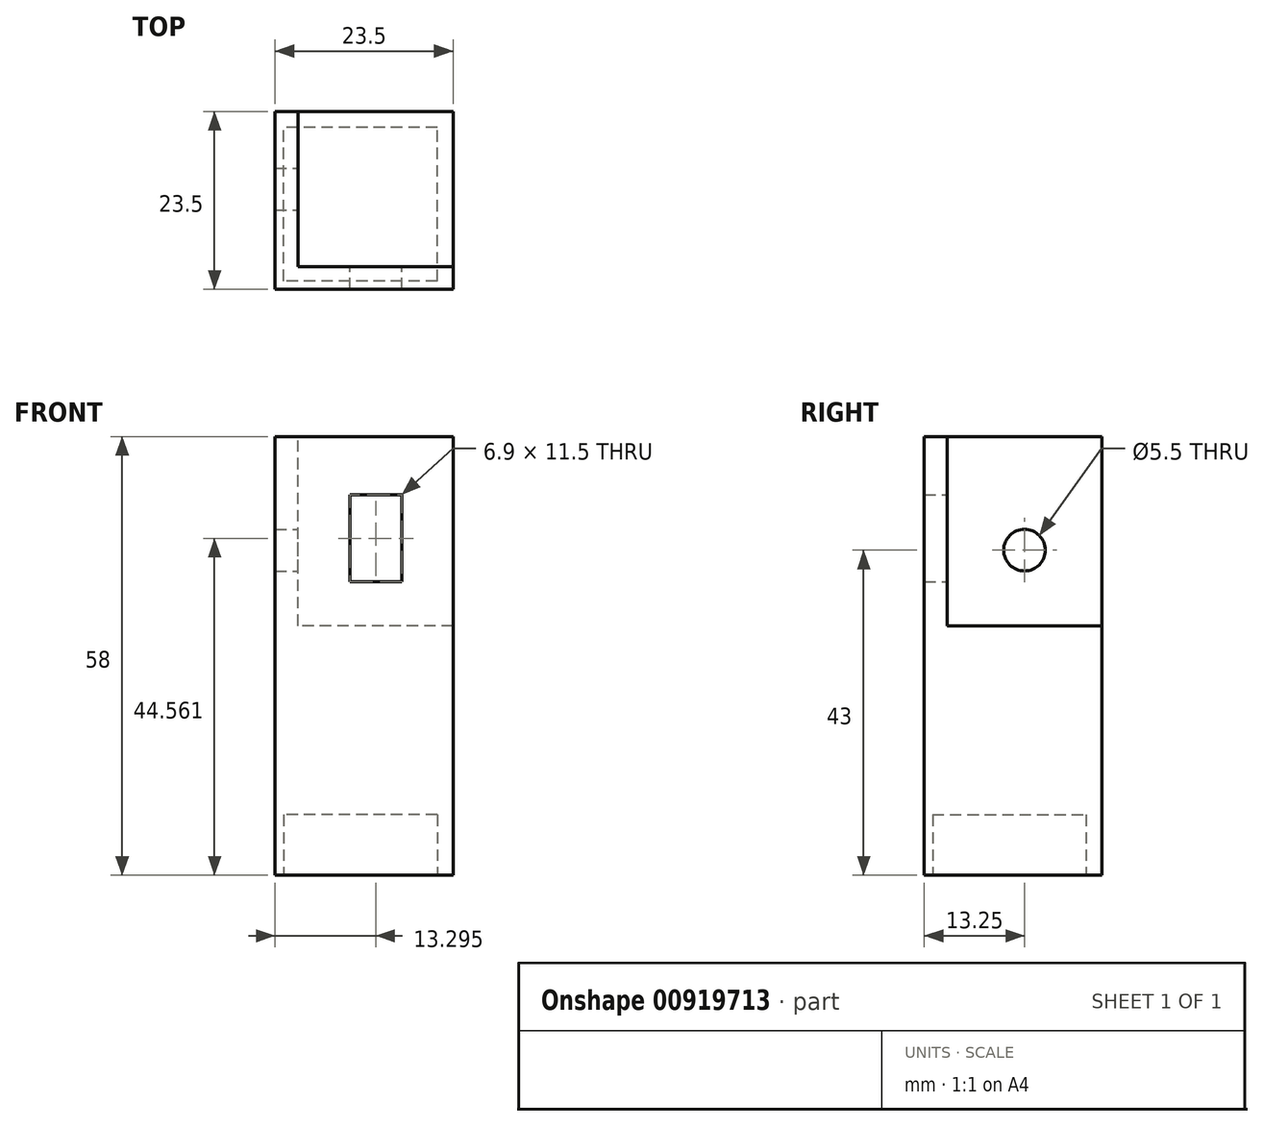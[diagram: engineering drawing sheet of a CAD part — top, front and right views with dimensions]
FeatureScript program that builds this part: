
annotation { "Feature Type Name" : "Feature", "Feature Type Description" : "" }
export const myFeature = defineFeature(function(context is Context, id is Id, definition is map)
    precondition{}
    {
        {
            var Q0;
            Q0=qCreatedBy(makeId("Top.planeOp"),FACE);
            var sketch = newSketch(context, id + "F0", { "sketchPlane" : qUnion([Q0])});
            skLineSegment(sketch, "E0.bottom", {"start": v(12.25, 12.25) * mm, "end": v(-12.25, 12.25) * mm});
            skLineSegment(sketch, "E0.top", {"start": v(12.25, -12.25) * mm, "end": v(-12.25, -12.25) * mm});
            skLineSegment(sketch, "E0.left", {"start": v(12.25, 12.25) * mm, "end": v(12.25, -12.25) * mm});
            skLineSegment(sketch, "E0.right", {"start": v(-12.25, 12.25) * mm, "end": v(-12.25, -12.25) * mm});
            skPoint(sketch, "E0.middle", {"position": v(0, 0) * mm});
            skSolve(sketch);
        }
        {
            var Q0;
            Q0=makeQuery(id+"F0.imprint","IMPRINT",FACE,{"disambiguationData":[TD([[makeQuery(id+"F0.imprint","IMPRINT",EDGE,{"derivedFrom":sQuery(id+"F0.wireOp",EDGE,"E0.bottom")}),1.0]])]});
            extrude(context, id + "F1", {"entities" : qUnion([Q0]), "depth" : 58 * mm, "offsetDistance" : 25 * mm});
        }
        {
            var Q0;
            Q0=makeQuery(id+"F1.opExtrude","CAP_FACE",FACE,{"disambiguationData":[OSD([sQuery(id+"F0.wireOp",EDGE,"E0.bottom"),sQuery(id+"F0.wireOp",EDGE,"E0.top"),sQuery(id+"F0.wireOp",EDGE,"E0.left"),sQuery(id+"F0.wireOp",EDGE,"E0.right")])],"isStart":true});
            var sketch = newSketch(context, id + "F2", { "sketchPlane" : qUnion([Q0])});
            skLineSegment(sketch, "E1.bottom", {"start": v(10.15, 10.15) * mm, "end": v(-10.15, 10.15) * mm});
            skLineSegment(sketch, "E1.top", {"start": v(10.15, -10.15) * mm, "end": v(-10.15, -10.15) * mm});
            skLineSegment(sketch, "E1.left", {"start": v(10.15, 10.15) * mm, "end": v(10.15, -10.15) * mm});
            skLineSegment(sketch, "E1.right", {"start": v(-10.15, 10.15) * mm, "end": v(-10.15, -10.15) * mm});
            skPoint(sketch, "E1.middle", {"position": v(0, 0) * mm});
            skSolve(sketch);
        }
        {
            var Q0;
            Q0 = qSketchRegion(id + "F2", true);
            extrude(context, id + "F3", {"entities" : qUnion([Q0]), "operationType" : NewBodyOperationType.REMOVE, "oppositeDirection" : true, "depth" : 6 * mm, "offsetDistance" : 25 * mm});
        }
        {
            var Q0;
            Q0=makeQuery(id+"F1.opExtrude","CAP_FACE",FACE,{"disambiguationData":[OSD([sQuery(id+"F0.wireOp",EDGE,"E0.bottom"),sQuery(id+"F0.wireOp",EDGE,"E0.top"),sQuery(id+"F0.wireOp",EDGE,"E0.left"),sQuery(id+"F0.wireOp",EDGE,"E0.right")])],"isStart":false});
            var sketch = newSketch(context, id + "F4", { "sketchPlane" : qUnion([Q0])});
            skLineSegment(sketch, "E2.bottom", {"start": v(12.25, 12.25) * mm, "end": v(-8.25, 12.25) * mm});
            skLineSegment(sketch, "E2.top", {"start": v(12.25, -8.25) * mm, "end": v(-8.25, -8.25) * mm});
            skLineSegment(sketch, "E2.left", {"start": v(12.25, 12.25) * mm, "end": v(12.25, -8.25) * mm});
            skLineSegment(sketch, "E2.right", {"start": v(-8.25, 12.25) * mm, "end": v(-8.25, -8.25) * mm});
            skSolve(sketch);
        }
        {
            var Q0;
            Q0=makeQuery(id+"F4.imprint","IMPRINT",FACE,{"disambiguationData":[TD([[makeQuery(id+"F4.imprint","IMPRINT",EDGE,{"derivedFrom":sQuery(id+"F4.wireOp",EDGE,"E2.bottom")}),1.0]])]});
            extrude(context, id + "F5", {"entities" : qUnion([Q0]), "operationType" : NewBodyOperationType.REMOVE, "oppositeDirection" : true, "depth" : 30 * mm, "offsetDistance" : 25 * mm});
        }
        {
            var Q0;
            Q0=makeQuery(id+"F5.boolean.opBoolean","COPY",FACE,{"derivedFrom":makeQuery(id+"F5.opExtrude","SWEPT_FACE",FACE,{"disambiguationData":[OSD([sQuery(id+"F4.wireOp",EDGE,"E2.right")])]})});
            var sketch = newSketch(context, id + "F6", { "sketchPlane" : qUnion([Q0])});
            skLineSegment(sketch, "E3", {"start": v(-8.25, 58) * mm, "end": v(12.25, 28) * mm, "construction": true});
            skLineSegment(sketch, "E4", {"start": v(12.25, 28) * mm, "end": v(-8.25, 28) * mm, "construction": true});
            skLineSegment(sketch, "E5", {"start": v(-8.25, 28) * mm, "end": v(12.25, 58) * mm, "construction": true});
            skPoint(sketch, "E6", {"position": v(2, 43) * mm});
            skSolve(sketch);
        }
        {
            var Q0;
            Q0=sQuery(id+"F6.wireOp",VERTEX,"E6");
            var Q1;
            Q1=makeQuery(id+"F1.opExtrude","SWEPT_BODY",BODY,{"disambiguationData":[OSD([sQuery(id+"F0.wireOp",EDGE,"E0.bottom"),sQuery(id+"F0.wireOp",EDGE,"E0.top"),sQuery(id+"F0.wireOp",EDGE,"E0.left"),sQuery(id+"F0.wireOp",EDGE,"E0.right")])]});
            hole(context, id + "F7", {"style" : HoleStyle.SIMPLE, "endStyle" : HoleEndStyle.THROUGH, "holeDiameter" : 5.5 * mm, "majorDiameter" : 5 * mm, "isTappedThrough" : true, "tappedDepth" : 12 * mm, "tapClearance" : 3, "locations" : qUnion([Q0]), "scope" : qUnion([Q1])});
        }
        {
            var Q0;
            Q0=makeQuery(id+"F5.boolean.opBoolean","COPY",FACE,{"derivedFrom":makeQuery(id+"F5.opExtrude","SWEPT_FACE",FACE,{"disambiguationData":[OSD([sQuery(id+"F4.wireOp",EDGE,"E2.top")])]})});
            var sketch = newSketch(context, id + "F8", { "sketchPlane" : qUnion([Q0])});
            skLineSegment(sketch, "E7", {"start": v(8.25, 58) * mm, "end": v(8.25, 28) * mm, "construction": true});
            skPoint(sketch, "E8", {"position": v(-2.04, 43.81) * mm});
            skLineSegment(sketch, "E9.bottom", {"start": v(1.16, 48.81) * mm, "end": v(-5.24, 48.81) * mm});
            skLineSegment(sketch, "E9.top", {"start": v(1.16, 38.81) * mm, "end": v(-5.24, 38.81) * mm});
            skLineSegment(sketch, "E9.left", {"start": v(1.16, 48.81) * mm, "end": v(1.16, 38.81) * mm});
            skLineSegment(sketch, "E9.right", {"start": v(-5.24, 48.81) * mm, "end": v(-5.24, 38.81) * mm});
            skSolve(sketch);
        }
        {
            var Q0;
            Q0 = qSketchRegion(id + "F8", true);
            extrude(context, id + "F9", {"entities" : qUnion([Q0]), "operationType" : NewBodyOperationType.REMOVE, "oppositeDirection" : true, "depth" : 25 * mm, "offsetDistance" : 25 * mm});
        }
        {
            var Q0;
            Q0=makeQuery(id+"F5.boolean.opBoolean","COPY",FACE,{"derivedFrom":makeQuery(id+"F5.opExtrude","CAP_FACE",FACE,{"disambiguationData":[OSD([sQuery(id+"F4.wireOp",EDGE,"E2.bottom"),sQuery(id+"F4.wireOp",EDGE,"E2.top"),sQuery(id+"F4.wireOp",EDGE,"E2.left"),sQuery(id+"F4.wireOp",EDGE,"E2.right")])],"isStart":false})});
            extrude(context, id + "F10", {"entities" : qUnion([Q0]), "operationType" : NewBodyOperationType.ADD, "depth" : 5 * mm, "offsetDistance" : 25 * mm});
        }
        {
            var Q0;
            Q0=makeQuery(id+"F9.boolean.opBoolean","COPY",FACE,{"derivedFrom":makeQuery(id+"F9.opExtrude","SWEPT_FACE",FACE,{"disambiguationData":[OSD([sQuery(id+"F8.wireOp",EDGE,"E9.left")])]})});
            extrude(context, id + "F11", {"entities" : qUnion([Q0]), "operationType" : NewBodyOperationType.REMOVE, "oppositeDirection" : true, "depth" : .25 * mm, "offsetDistance" : 25 * mm});
        }
        {
            var Q0;
            Q0=makeQuery(id+"F9.boolean.opBoolean","COPY",FACE,{"derivedFrom":makeQuery(id+"F9.opExtrude","SWEPT_FACE",FACE,{"disambiguationData":[OSD([sQuery(id+"F8.wireOp",EDGE,"E9.right")])]})});
            extrude(context, id + "F12", {"entities" : qUnion([Q0]), "operationType" : NewBodyOperationType.REMOVE, "oppositeDirection" : true, "depth" : .25 * mm, "offsetDistance" : 25 * mm});
        }
        {
            var Q0;
            {var subQ0=sQuery(id+"F8.wireOp",EDGE,"E9.bottom");Q0=makeQuery(id+"F12.boolean.opBoolean","MERGE",FACE,{"derivedFrom":[makeQuery(id+"F11.boolean.opBoolean","MERGE",FACE,{"derivedFrom":[makeQuery(id+"F9.boolean.opBoolean","COPY",FACE,{"derivedFrom":makeQuery(id+"F9.opExtrude","SWEPT_FACE",FACE,{"disambiguationData":[OSD([subQ0])]})})],"fromTools":[makeQuery(id+"F11.opExtrude","SWEPT_FACE",FACE,{"disambiguationData":[OSD([subQ0,sQuery(id+"F8.wireOp",EDGE,"E9.left")])]})]})],"fromTools":[makeQuery(id+"F12.opExtrude","SWEPT_FACE",FACE,{"disambiguationData":[OSD([subQ0,sQuery(id+"F8.wireOp",EDGE,"E9.right")])]})]});}
            extrude(context, id + "F13", {"entities" : qUnion([Q0]), "operationType" : NewBodyOperationType.REMOVE, "oppositeDirection" : true, "depth" : 1.5 * mm, "offsetDistance" : 25 * mm});
        }
        {
            var Q0;
            Q0=makeQuery(id+"F1.opExtrude","SWEPT_FACE",FACE,{"disambiguationData":[OSD([sQuery(id+"F0.wireOp",EDGE,"E0.right")])]});
            extrude(context, id + "F14", {"entities" : qUnion([Q0]), "operationType" : NewBodyOperationType.REMOVE, "oppositeDirection" : true, "depth" : 1 * mm, "offsetDistance" : 25 * mm});
        }
        {
            var Q0;
            Q0=makeQuery(id+"F1.opExtrude","SWEPT_FACE",FACE,{"disambiguationData":[OSD([sQuery(id+"F0.wireOp",EDGE,"E0.top")])]});
            extrude(context, id + "F15", {"entities" : qUnion([Q0]), "operationType" : NewBodyOperationType.REMOVE, "oppositeDirection" : true, "depth" : 1 * mm, "offsetDistance" : 25 * mm});
        }
        {
            var Q0;
            Q0=makeQuery(id+"F3.boolean.opBoolean","COPY",FACE,{"derivedFrom":makeQuery(id+"F3.opExtrude","CAP_FACE",FACE,{"disambiguationData":[OSD([sQuery(id+"F2.wireOp",EDGE,"E1.bottom"),sQuery(id+"F2.wireOp",EDGE,"E1.top"),sQuery(id+"F2.wireOp",EDGE,"E1.left"),sQuery(id+"F2.wireOp",EDGE,"E1.right")])],"isStart":false})});
            extrude(context, id + "F16", {"entities" : qUnion([Q0]), "operationType" : NewBodyOperationType.REMOVE, "oppositeDirection" : true, "depth" : 2 * mm, "offsetDistance" : 25 * mm});
        }
    });
